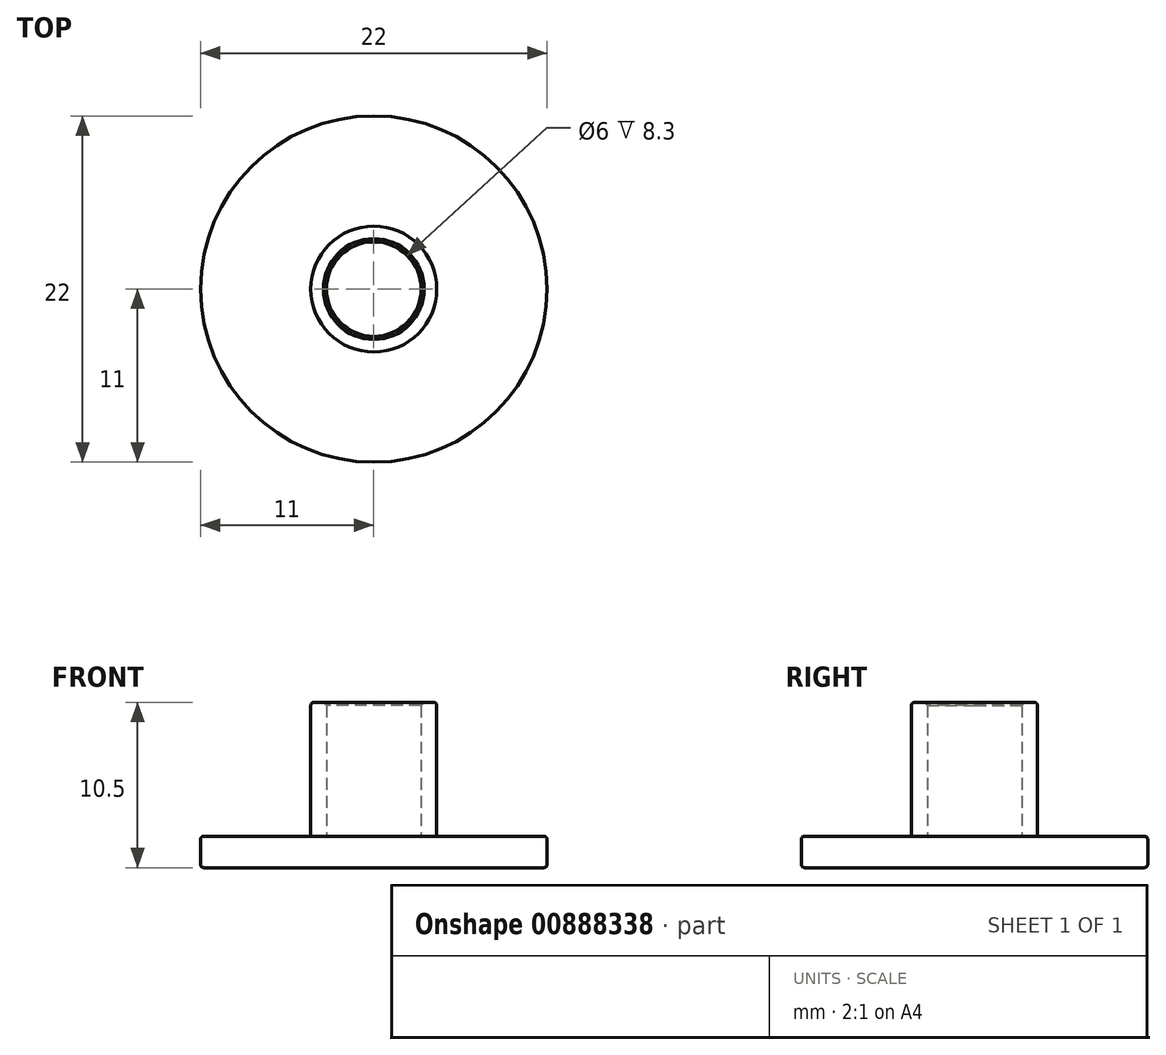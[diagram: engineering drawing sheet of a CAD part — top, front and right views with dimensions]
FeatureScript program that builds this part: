
annotation { "Feature Type Name" : "Feature", "Feature Type Description" : "" }
export const myFeature = defineFeature(function(context is Context, id is Id, definition is map)
    precondition{}
    {
        {
            var Q0;
            Q0=qCreatedBy(makeId("Top.planeOp"),FACE);
            var sketch = newSketch(context, id + "F0", { "sketchPlane" : qUnion([Q0])});
            skCircle(sketch, "E0", {"center": v(0, 0) * mm, "radius": 11 * mm});
            skSolve(sketch);
        }
        {
            var Q0;
            Q0 = qSketchRegion(id + "F0", true);
            extrude(context, id + "F1", {"entities" : qUnion([Q0]), "depth" : 2 * mm, "offsetDistance" : 25.4 * mm});
        }
        {
            var Q0;
            Q0=makeQuery(id+"F1.opExtrude","CAP_FACE",FACE,{"disambiguationData":[OSD([sQuery(id+"F0.wireOp",EDGE,"E0")])],"isStart":false});
            var sketch = newSketch(context, id + "F2", { "sketchPlane" : qUnion([Q0])});
            skCircle(sketch, "E1", {"center": v(0, 0) * mm, "radius": 4 * mm});
            skCircle(sketch, "E2", {"center": v(0, 0) * mm, "radius": 3 * mm});
            skSolve(sketch);
        }
        {
            var Q0;
            Q0=makeQuery(id+"F2.imprint","IMPRINT",FACE,{"disambiguationData":[TD([[makeQuery(id+"F2.imprint","IMPRINT",EDGE,{"derivedFrom":sQuery(id+"F2.wireOp",EDGE,"E1")}),1.0]])]});
            extrude(context, id + "F3", {"entities" : qUnion([Q0]), "operationType" : NewBodyOperationType.ADD, "depth" : 8.5 * mm, "offsetDistance" : 25.4 * mm});
        }
        {
            var Q0;
            Q0=makeQuery(id+"F3.opExtrude","CAP_EDGE",EDGE,{"disambiguationData":[OSD([sQuery(id+"F2.wireOp",EDGE,"E1")])],"isStart":false});
            var Q1;
            Q1=makeQuery(id+"F1.opExtrude","CAP_EDGE",EDGE,{"disambiguationData":[OSD([sQuery(id+"F0.wireOp",EDGE,"E0")])],"isStart":false});
            var Q2;
            Q2=makeQuery(id+"F1.opExtrude","CAP_EDGE",EDGE,{"disambiguationData":[OSD([sQuery(id+"F0.wireOp",EDGE,"E0")])],"isStart":true});
            fillet(context, id + "F4", {"entities" : qUnion([Q0, Q1, Q2]), "radius" : .2 * mm, "tangentPropagation" : true, "allowEdgeOverflow" : false});
        }
        {
            var Q0;
            Q0=makeQuery(id+"F3.opExtrude","CAP_EDGE",EDGE,{"disambiguationData":[OSD([sQuery(id+"F2.wireOp",EDGE,"E2")])],"isStart":false});
            chamfer(context, id + "F5", {"entities" : qUnion([Q0]), "width" : 0.2 * mm, "tangentPropagation" : true});
        }
    });
